# Revit family: Door_Access_Floor_Best_Access_Doors_BA-HFR-18-Carpet-VinylTile
name_source: partatom
category: Specialty Equipment
revit_build: Autodesk Revit 2017 (Build: 20160225_1515(x64)
units: mm (PartAtom-declared; Revit-internal decimal feet)

## family parameters
Cut with Voids When Loaded = No
Host = Face
Part Type = Normal
Room Calculation Point = No
Round Connector Dimension = Use Diameter
Shared = No

## types (1)
- Door_Access_Floor_Best_Access_Doors_BA-HFR-18-Carpet-VinylTile
    Capacity = as Specified
    Clear Opening Height = 2' - 0"
    Clear Opening Width = 1' - 8"
    Default Elevation = 0' - 0"
    Description = Best Access Doors Product as Specified
    Door Height = 2' - 1 1/8"
    Door Width = 1' - 10 3/4"
    Double Leaf = No
    Expected Lifespan (Years) = 0
    Maintenance Schedule (Months) = 0
    Manufacturer = Best Access Doors
    Model = As Specified
    Opening Height = 2' - 1 1/8"
    Opening Width = 1' - 10 3/4"
    Overall Height = 2' - 7 1/8"
    Overall Width = 2' - 4 3/4"
    Product data url = https://bimobject.com
    Revision = R1_2017-03
    Single Leaf = Yes
    Standards Conformance = as Specified
    URL = https://www.bestaccessdoors.com
    Unit Depth = 0' - 3"
    Unit Height = 2' - 1 1/8"
    Unit Weight = 0
    Unit Width = 1' - 10 3/4"
    Warranty Duration (Years) = 0
    halfswing = 0' - 11 3/8"
    singleleafframelocate = 0' - 3"

## geometry (parser evidence)
native form markers: Sweep x6
no freeform markers — native parametric forms only
